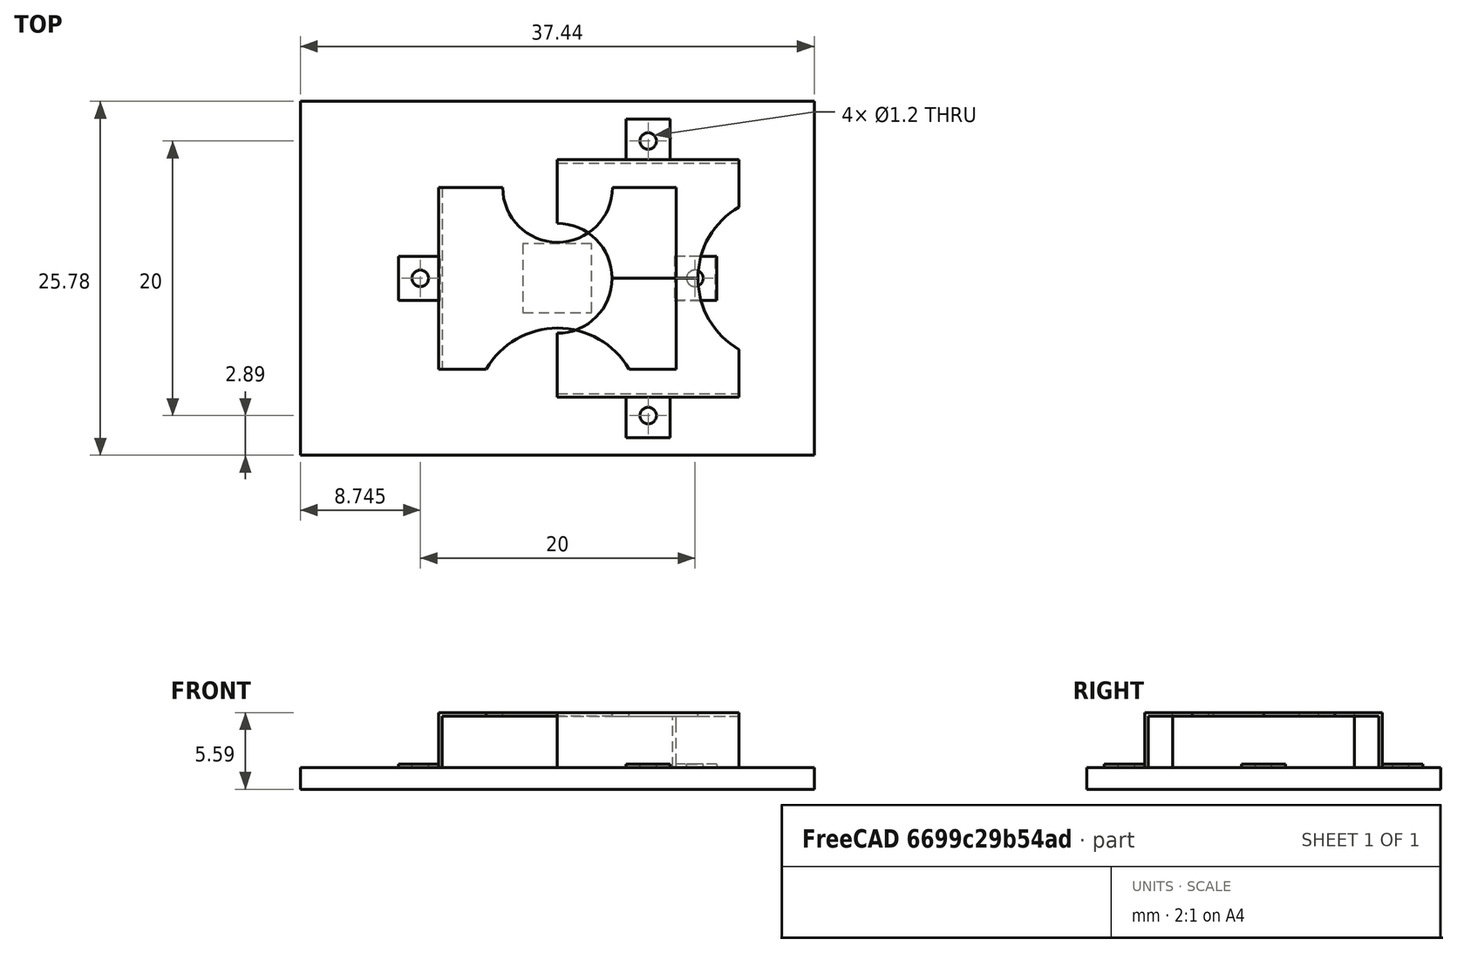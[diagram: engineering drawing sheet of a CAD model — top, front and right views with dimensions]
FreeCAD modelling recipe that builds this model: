
FCSTD DOCUMENT  (FreeCAD 0.19R18353 (Git))
Label: SMTM1632
License: All rights reserved
LicenseURL: http://en.wikipedia.org/wiki/All_rights_reserved
objects: Part::Cut×14, Part::Box×10, Part::Cylinder×6, Part::FeaturePython×4, Part::Mirroring×1, App::DocumentObjectGroup×1, Part::Feature×1
note: 36 computed .brp shape members not serialized (recipe doc carries the construction recipe); baked Part::Feature solids carry a one-line shape summary decoded from their .brp

FEATURE [Part::Box] cube
  AttacherType = Attacher::AttachEngine3D
  Height = 4
  Length = 13.25
  Width = 11.6
FEATURE [Part::Box] cube001
  AttacherType = Attacher::AttachEngine3D
  Height = 4
  Length = 15.25
  Placement = pos=(-1,-1,0.25) rot=(0,0,1;0rad)
  Width = 3.95
FEATURE [Part::Cut] difference
  Base = -> cube
  Placement = pos=(0,-11.6,0) rot=(0,0,1;0rad)
  Tool = -> cube001
FEATURE [Part::Box] cube002
  AttacherType = Attacher::AttachEngine3D
  Height = 4
  Length = 15.25
  Placement = pos=(-1,-8.4,-0.25) rot=(0,0,1;0rad)
  Width = 11.6
FEATURE [Part::Cut] difference001
  Base = -> difference
  Tool = -> cube002
FEATURE [Part::Box] cube003
  AttacherType = Attacher::AttachEngine3D
  Height = 4
  Length = 6.025
  Placement = pos=(-1,-12.6,-1) rot=(0,0,1;0rad)
  Width = 3.95
FEATURE [Part::Cut] difference002
  Base = -> difference001
  Tool = -> cube003
FEATURE [Part::Box] cube004
  AttacherType = Attacher::AttachEngine3D
  Height = 4
  Length = 6.025
  Placement = pos=(8.225,-12.6,-1) rot=(0,0,1;0rad)
  Width = 3.95
FEATURE [Part::Cut] difference003
  Base = -> difference002
  Tool = -> cube004
FEATURE [Part::Cylinder] cylinder
  Angle = 360
  AttacherType = Attacher::AttachEngine3D
  Height = 6
  Radius = 4
FEATURE [Part::Cut] difference004
  Base = -> difference003
  Tool = -> cylinder
FEATURE [Part::Cylinder] cylinder001
  Angle = 360
  AttacherType = Attacher::AttachEngine3D
  Height = 6
  Placement = pos=(16.25,0,0) rot=(0,0,1;0rad)
  Radius = 6
FEATURE [Part::Cut] difference005
  Base = -> difference004
  Tool = -> cylinder001
FEATURE [Part::Cylinder] cylinder002
  Angle = 360
  AttacherType = Attacher::AttachEngine3D
  Height = 4
  Placement = pos=(6.625,-10,-1) rot=(0,0,1;0rad)
  Radius = 0.6
FEATURE [Part::Cut] difference006
  Base = -> difference005
  Tool = -> cylinder002
FEATURE [Part::Box] cube005
  AttacherType = Attacher::AttachEngine3D
  Height = 4
  Length = 13.25
  Width = 11.6
FEATURE [Part::Box] cube006
  AttacherType = Attacher::AttachEngine3D
  Height = 4
  Length = 15.25
  Placement = pos=(-1,-1,0.25) rot=(0,0,1;0rad)
  Width = 3.95
FEATURE [Part::Cut] difference007
  Base = -> cube005
  Placement = pos=(0,-11.6,0) rot=(0,0,1;0rad)
  Tool = -> cube006
FEATURE [Part::Box] cube007
  AttacherType = Attacher::AttachEngine3D
  Height = 4
  Length = 15.25
  Placement = pos=(-1,-8.4,-0.25) rot=(0,0,1;0rad)
  Width = 11.6
FEATURE [Part::Cut] difference008
  Base = -> difference007
  Tool = -> cube007
FEATURE [Part::Box] cube008
  AttacherType = Attacher::AttachEngine3D
  Height = 4
  Length = 6.025
  Placement = pos=(-1,-12.6,-1) rot=(0,0,1;0rad)
  Width = 3.95
FEATURE [Part::Cut] difference009
  Base = -> difference008
  Tool = -> cube008
FEATURE [Part::Box] cube009
  AttacherType = Attacher::AttachEngine3D
  Height = 4
  Length = 6.025
  Placement = pos=(8.225,-12.6,-1) rot=(0,0,1;0rad)
  Width = 3.95
FEATURE [Part::Cut] difference010
  Base = -> difference009
  Tool = -> cube009
FEATURE [Part::Cylinder] cylinder003
  Angle = 360
  AttacherType = Attacher::AttachEngine3D
  Height = 6
  Radius = 4
FEATURE [Part::Cut] difference011
  Base = -> difference010
  Tool = -> cylinder003
FEATURE [Part::Cylinder] cylinder004
  Angle = 360
  AttacherType = Attacher::AttachEngine3D
  Height = 6
  Placement = pos=(16.25,0,0) rot=(0,0,1;0rad)
  Radius = 6
FEATURE [Part::Cut] difference012
  Base = -> difference011
  Tool = -> cylinder004
FEATURE [Part::Cylinder] cylinder005
  Angle = 360
  AttacherType = Attacher::AttachEngine3D
  Height = 4
  Placement = pos=(6.625,-10,-1) rot=(0,0,1;0rad)
  Radius = 0.6
FEATURE [Part::Cut] difference013
  Base = -> difference012
  Tool = -> cylinder005
FEATURE [Part::Mirroring] mirr_difference013  label="mirrored difference013"
  Base = (0,0,0)
  Normal = (0,1,0)
  Source = -> difference013
FEATURE [Part::FeaturePython] FCrtYd_lines  label="FCrtYd"  # a2plus imported part (geometry in sourceFile) (typed FeaturePython)
  fixedPosition = true
FEATURE [Part::FeaturePython] Filk_lines  label="FrontSilk"  # a2plus imported part (geometry in sourceFile) (typed FeaturePython)
  fixedPosition = true
FEATURE [Part::FeaturePython] TopPads  # a2plus imported part (geometry in sourceFile) (typed FeaturePython)
  fixedPosition = true
FEATURE [Part::FeaturePython] newPCB  label="Pcb"  # a2plus imported part (geometry in sourceFile) (typed FeaturePython)
  fixedPosition = true
FEATURE [App::DocumentObjectGroup] SMTM1632_fp
  Group = -> [FCrtYd_lines,Filk_lines,TopPads,newPCB]
FEATURE [Part::Feature] Shape  label="Fusion"
  shape: bbox 23.2 x 13.25 x 4 mm, 36 faces (baked)
